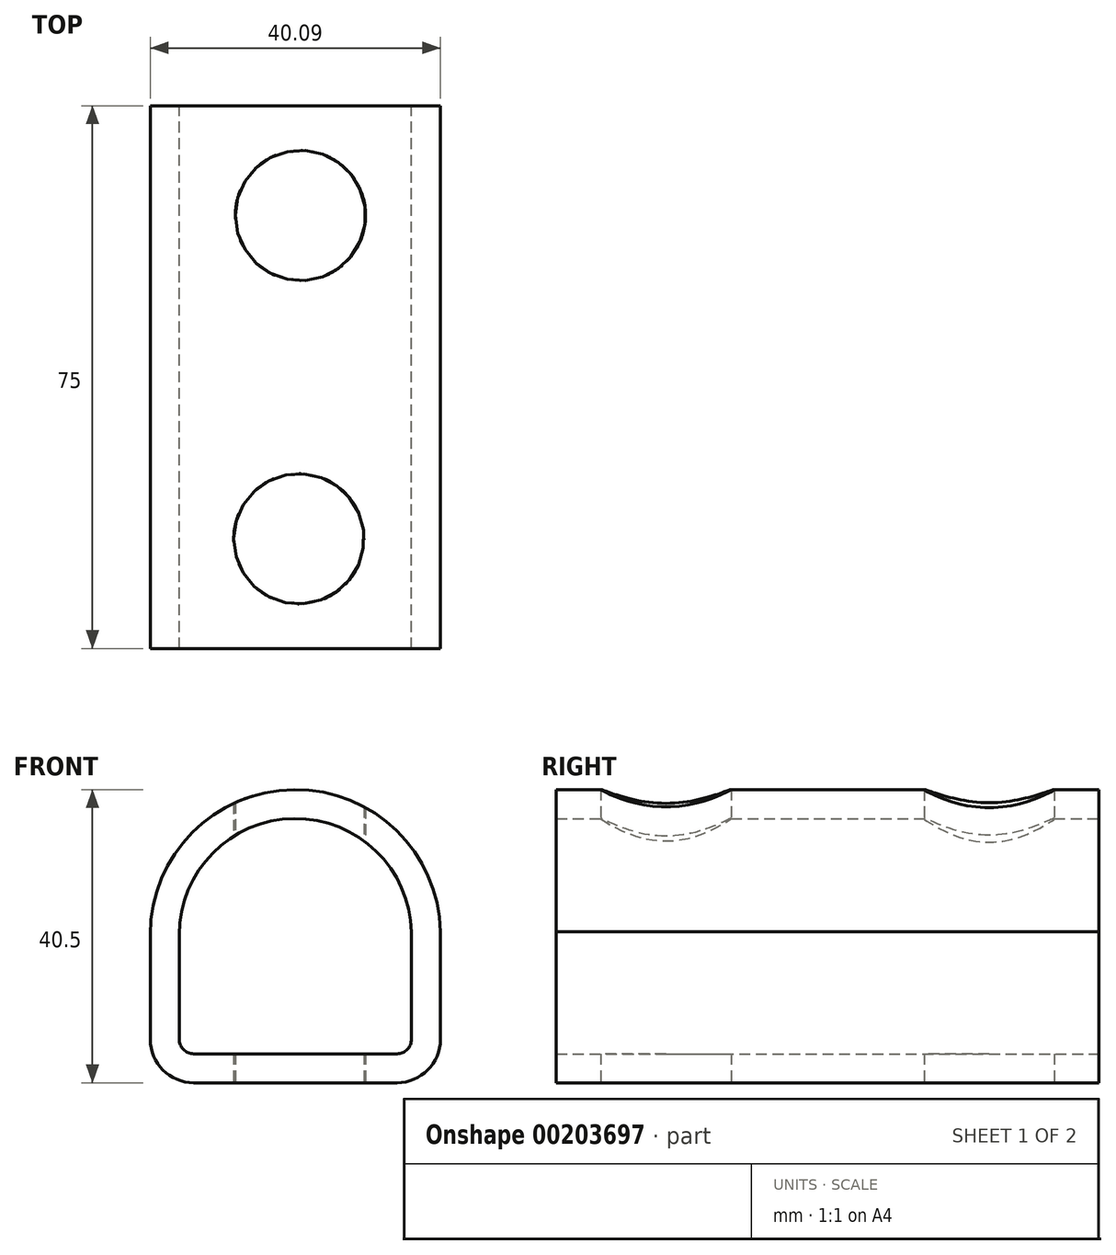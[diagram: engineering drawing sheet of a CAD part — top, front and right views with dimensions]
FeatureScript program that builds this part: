
annotation { "Feature Type Name" : "Feature", "Feature Type Description" : "" }
export const myFeature = defineFeature(function(context is Context, id is Id, definition is map)
    precondition{}
    {
        {
            var Q0;
            Q0=qCreatedBy(makeId("Front.planeOp"),FACE);
            var sketch = newSketch(context, id + "F0", { "sketchPlane" : qUnion([Q0])});
            skLineSegment(sketch, "E0", {"start": v(-38.1, -11.55) * mm, "end": v(1.99, -11.55) * mm});
            skLineSegment(sketch, "E1", {"start": v(-38.1, -11.55) * mm, "end": v(-38.1, 8.9) * mm});
            skLineSegment(sketch, "E2", {"start": v(1.99, -11.55) * mm, "end": v(1.99, 9.29) * mm});
            skArc(sketch, "E3", {"start": v(1.99, 9.29) * mm, "mid": v(-18.24, 28.95) * mm, "end": v(-38.1, 8.9) * mm});
            skSolve(sketch);
        }
        {
            var Q0;
            Q0 = qSketchRegion(id + "F0", true);
            extrude(context, id + "F1", {"entities" : qUnion([Q0]), "depth" : 75 * mm});
        }
        {
            var Q0;
            Q0=makeQuery(id+"F1.opExtrude","SWEPT_EDGE",EDGE,{"disambiguationData":[OSD([sQuery(id+"F0.wireOp",EDGE,"E0"),sQuery(id+"F0.wireOp",EDGE,"E2")])]});
            var Q1;
            Q1=makeQuery(id+"F1.opExtrude","SWEPT_EDGE",EDGE,{"disambiguationData":[OSD([sQuery(id+"F0.wireOp",EDGE,"E0"),sQuery(id+"F0.wireOp",EDGE,"E1")])]});
            fillet(context, id + "F2", {"entities" : qUnion([Q0, Q1]), "radius" : 6 * mm, "tangentPropagation" : true, "allowEdgeOverflow" : false});
        }
        {
            var Q0;
            Q0=makeQuery(id+"F1.opExtrude","CAP_FACE",FACE,{"disambiguationData":[OSD([sQuery(id+"F0.wireOp",EDGE,"E0"),sQuery(id+"F0.wireOp",EDGE,"E1"),sQuery(id+"F0.wireOp",EDGE,"E2"),sQuery(id+"F0.wireOp",EDGE,"E3")])],"isStart":false});
            var Q1;
            Q1=makeQuery(id+"F1.opExtrude","CAP_FACE",FACE,{"disambiguationData":[OSD([sQuery(id+"F0.wireOp",EDGE,"E0"),sQuery(id+"F0.wireOp",EDGE,"E1"),sQuery(id+"F0.wireOp",EDGE,"E2"),sQuery(id+"F0.wireOp",EDGE,"E3")])],"isStart":true});
            shell(context, id + "F3", {"entities" : qUnion([Q0, Q1]), "thickness" : 4 * mm});
        }
        {
            var Q0;
            Q0=makeQuery(id+"F1.opExtrude","SWEPT_FACE",FACE,{"disambiguationData":[OSD([sQuery(id+"F0.wireOp",EDGE,"E0")])]});
            var sketch = newSketch(context, id + "F4", { "sketchPlane" : qUnion([Q0])});
            skLineSegment(sketch, "E4.bottom", {"start": v(-38.1, 75) * mm, "end": v(-17.57, 75) * mm});
            skLineSegment(sketch, "E4.top", {"start": v(-38.1, 59.84) * mm, "end": v(-17.57, 59.84) * mm});
            skLineSegment(sketch, "E4.left", {"start": v(-38.1, 75) * mm, "end": v(-38.1, 59.84) * mm});
            skLineSegment(sketch, "E4.right", {"start": v(-17.57, 75) * mm, "end": v(-17.57, 59.84) * mm});
            skSolve(sketch);
        }
        {
            var Q0;
            Q0=sQuery(id+"F4.wireOp",VERTEX,"E4.top.end");
            var Q1;
            Q1=makeQuery(id+"F1.opExtrude","SWEPT_BODY",BODY,{"disambiguationData":[OSD([sQuery(id+"F0.wireOp",EDGE,"E0"),sQuery(id+"F0.wireOp",EDGE,"E1"),sQuery(id+"F0.wireOp",EDGE,"E2"),sQuery(id+"F0.wireOp",EDGE,"E3")])]});
            hole(context, id + "F5", {"style" : HoleStyle.SIMPLE, "endStyle" : HoleEndStyle.THROUGH, "holeDiameter" : 18 * mm, "locations" : qUnion([Q0]), "scope" : qUnion([Q1]), "isTappedThrough" : true});
        }
        {
            var Q0;
            Q0=makeQuery(id+"F1.opExtrude","SWEPT_FACE",FACE,{"disambiguationData":[OSD([sQuery(id+"F0.wireOp",EDGE,"E0")])]});
            var sketch = newSketch(context, id + "F6", { "sketchPlane" : qUnion([Q0])});
            skLineSegment(sketch, "E5.bottom", {"start": v(-38.1, 0) * mm, "end": v(-17.35, 0) * mm});
            skLineSegment(sketch, "E5.top", {"start": v(-38.1, 15.16) * mm, "end": v(-17.35, 15.16) * mm});
            skLineSegment(sketch, "E5.left", {"start": v(-38.1, 0) * mm, "end": v(-38.1, 15.16) * mm});
            skLineSegment(sketch, "E5.right", {"start": v(-17.35, 0) * mm, "end": v(-17.35, 15.16) * mm});
            skSolve(sketch);
        }
        {
            var Q0;
            Q0=sQuery(id+"F6.wireOp",VERTEX,"E5.right.end");
            var Q1;
            Q1=makeQuery(id+"F1.opExtrude","SWEPT_BODY",BODY,{"disambiguationData":[OSD([sQuery(id+"F0.wireOp",EDGE,"E0"),sQuery(id+"F0.wireOp",EDGE,"E1"),sQuery(id+"F0.wireOp",EDGE,"E2"),sQuery(id+"F0.wireOp",EDGE,"E3")])]});
            hole(context, id + "F7", {"style" : HoleStyle.SIMPLE, "endStyle" : HoleEndStyle.THROUGH, "holeDiameter" : 18 * mm, "locations" : qUnion([Q0]), "scope" : qUnion([Q1]), "isTappedThrough" : true});
        }
    });
